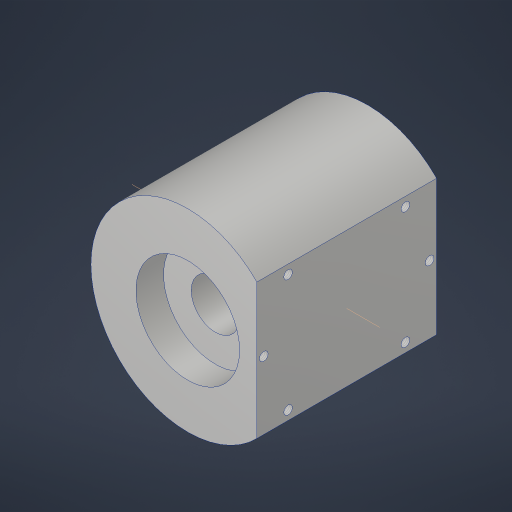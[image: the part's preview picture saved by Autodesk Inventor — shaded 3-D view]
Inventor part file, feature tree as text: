
AUTODESK INVENTOR PART (.ipt)
format: ipt  version: 2023.4 (Build 274418000, 418)  size: 235,520 bytes
history: native  units: in
note: dims shown in document units (in); Inventor stores cm internally (conversion verified against a paired STEP export)
features: sketch x5, extrude x4, projected_geometry x3, hole x1, other x1, pattern_circular x1
ambient origin geometry x8: Origin, YZ Plane, XZ Plane, XY Plane, X Axis, Y Axis, Z Axis, Center Point
bodies: Solid1 (feature_tree)
feature tree (15):
  extrude  "Extrusion1"  Depth=4.5in
  extrude  "Extrusion2"  Depth=0.25in
  extrude  "Extrusion3"  Depth=0.8358in
  hole  "Hole1"  [1 undecoded]
  other  "Work Axis1"
  pattern_circular  "Circular Pattern1"  [2 undecoded]
  extrude  "Extrusion4"  Depth=0.5in
  sketch  "Sketch1"  dims[d0=0.875in d2=4.5in]
  sketch  "Sketch3"  dims[d3=3.5in d4=0.25in]
  sketch  "Sketch4"  dims[d5=1.4142in d6=0.8358in]
  sketch  "Sketch5"  dims[d7=1.25in d8=3.25in d9=0.0in]
  sketch  "Sketch6"  dims[d10=1.875in d11=0.5in d12=0.0in d13=1.875in d14=0.5in d15=0.0in d16=3.0in d17=0.156in d18=0.38in d19=0.385in d20=0.25in d21=0.5635in d22=0.536in d23=0.0in d24=3.1496in d25=360.0deg d27=0.5in d28=1.0in d29=0.0in d30=3.1496in d32=360.0deg]
  projected_geometry  "Project Cut Edges1"
  projected_geometry  "Project Cut Edges2"
  projected_geometry  "Project Cut Edges3"
note: 3 required parameter values undecoded (feature->parameter linkage not recoverable at this tier; creation-order binding heuristic only, values carry confidence <= 0.55)
